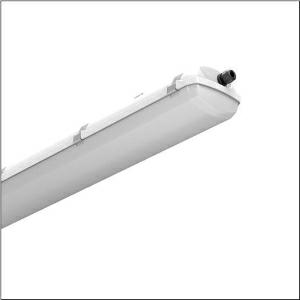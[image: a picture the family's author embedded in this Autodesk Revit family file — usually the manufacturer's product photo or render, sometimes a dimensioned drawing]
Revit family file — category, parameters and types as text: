
# Revit family: monsun_r__ex_51fxb2dl480a_525c
name_source: partatom
category: Lighting Fixtures
units: mm (PartAtom-declared; Revit-internal decimal feet)

## family parameters
Cut with Voids When Loaded = No
Host = Face
Light Source = No
Part Type = Normal
Room Calculation Point = No
Round Connector Dimension = Use Diameter
Shared = No

## types (1)
- Monsun® Ex (1 x LED, 8720 lm, 58.4 W, 4000K)
    Apparent Load = 58 VA
    CIE Flux Codes = 43 72 91 92 100
    Color Rendering = 80
    Color Temperature = 4000K
    Default Elevation = 1800 mm
    Description = Monsun® Ex, damp-proof luminaire, primary optical cover: cover, of PC, UV-stabilised, opal, light emission: direct distribution, primary light characteristic: symmetric, installation type: surface-mounted, LED, rated luminous flux: 8.720lm, luminous efficacy: 149lm/W, light colour: 840, colour temperature: 4000K, control gear: DALI 2, with terminal, 5-pole, max. 2.5mm², through-wiring: 7x 2.5mm², mains connection: 220..240V, AC, 50/60Hz, rated input power: 58W, housing, of PC, light grey (RAL 7035), incl. blanking plug, incl. 2x Ex cable gland M20 for cable diameter 7..12mm with sealing, length: 1.280mm, width: 155mm, height: 105mm, clip for enclosure, of stainless steel, protection rating (complete): IP66, insulation class (complete): insulation class I (protective earthing), certification: CE, explosion class: zone2,22 II 3G Ex nR IIC T6 GC, II 3D Ex tc IIIC T80°C Dc, impact resistance: IK10, permissible operating ambient temperature: -20..+60°C, LABS conformity tested according to VDMA 24364:2018-05, contact your sales advisor before using the luminaires in applications with unclear chemical exposure, large temperature fluctuations or condensation-forming humidity, packaging unit: 1 piece
    Height = 105 mm
    Lamp = 1 x LED
    Lamp Light Flux = 8720 lm
    Lamp Power = 58.4 W
    Lamp count = 1
    Length = 1280 mm
    Luminous efficacy = 149 lm/W
    Manufacturer = Siteco
    ModVariant = No
    Model = 51FXB2DL480A
    Mounting Place = Ceiling
    Mounting Type = Surface mounted
    Number of Poles = 1
    OnlyDefault = Yes
    Power Factor = 1
    Product Name = Monsun® Ex
    Product group = damp-proof luminaire
    ProductGroupID = 301
    Protection Class = Protection class I
    Protection Degree = IP 66
    RLX_Detail_Level = 1
    RLX_Emergency_Light_Flux = 0 lm
    RLX_Emergency_Type = 0
    RLX_Emergency_Type_DB = No
    RlxData = <blob elided: 41597 chars, md5=01f991c9>
    Socket = socket
    Standby Power = 0 W
    System Light Flux = 8720 lm
    System Power = 58 W
    Type Comments = Product without accessories
    Type Image = l_1258882.jpg
    URL = http://relux.com
    VarID = ---
    Voltage = 0 V
    Weight = 0.00 kg
    Width = 155 mm

## geometry (parser evidence)
native form markers: Blend x4, Sweep x13
no freeform markers — native parametric forms only
